# Revit family: Building-SurfaceMountingEnclosures-GEWISS-40CDK-ENCLOSURES_IP65_4X
name_source: partatom
category: Apparecchi elettrici
revit_build: Autodesk Revit 2016 (Build: 20161004_0715(x64)
units: mm (PartAtom-declared; Revit-internal decimal feet)

## family parameters
Condiviso = No
Host = Superficie
Mantenere orientamento annotazione = Sì
Numero OmniClass = 23.80.30.11.17
Punto di calcolo locali = Sì
Quota connettore circolare = Usa diametro
Taglio con vuoti quando caricato = No
Tipo di parte = Normale
Titolo OmniClass = Distribution Boards and Control Panels

## types (1)
- GW40109 - SUR. MOU. DISTRIB.BOARD 72M.(18X4) IP65
    Accessories for insulation restoring = Screwcaps (GW44623) or fixing brackets in resin (GW44621)
    Catalogue = BUILDING
    Catalogue Range = 40 CDK
    Colour = Grey RAL 7035
    Descrizione = SUR. MOU. DISTRIB.BOARD 72M.(18X4) IP65
    Diametro_tubazione = 30 mm  [stored 0.0984252 ft]
    Dimensione modulo = 18 mm  [stored 0.0590551 ft]
    Dispersible power (W) = 89
    Door colour = Smoked Transparent
    EAN code = 8011564062269
    Electrocod = 0321
    Glow Wire Test = 650°C
    H_finestratura = 45 mm  [stored 0.147638 ft]
    H_quadro = 878 mm  [stored 2.88058 ft]
    IDF = e275c9cb-e94d-4235-9db2-dc04921218fb
    IDT = 7e0685bc-1a66-4e12-9668-7a0b7038d661
    IP degree = IP65
    Insulation class = II (according to IEC 61140 standards)
    Insulation voltage: = 1000 V according to EN 62208 both in ac as well as in dc
    L_finestratura = 324 mm  [stored 1.06299 ft]
    L_quadro = 410 mm  [stored 1.34514 ft]
    Max. installable terminal blocks = 4 x 18 modules
    Modello = GW40109
    N.M. = 18
    No. of modules EN 50022 = 72 (18x4)
    No. of modules EN 50022: = 72 (18x4)
    Operating temperature = -25 +60 °C
    Outer dim. LxHxD (mm) = 410x878x160
    Produttore = GEWISS S.p.A.
    Prondita_quadro = 160 mm  [stored 0.524934 ft]
    Prospetto di default = 1219 mm
    QUADRO = FINITURA BIANCA
    Rated current: = 125A
    Rated insulation voltage (Ui) = 1000 V
    Rated voltage = 400V
    SEO = Board
    Shock resistance = IK09
    Spostamento_x_et = 1060 mm
    Standard = EN 60670-1 (CEI 23-48) IEC60670-24 CEI 23-49
    Standard. = EN 60670-1 (CEI 23-48) IEC60670-24 CEI 23-49
    Technical sheet = https://www.gewiss.com
    Thermo-pressure with ball = 70
    Type of material = Halogen-free in compliance with EN 60754-2
    URL = https://www.gewiss.com
    Version file RFA = 18.0
    fase1 = 0 VA
    h_pannello = 718 mm  [stored 2.35564 ft]
    voltaggio_quadro = 0 V

note: source unit labels omitted for Thermo-pressure with ball — the stored unit's dimension contradicts the parameter name (converter mislabeling)

note: [stored X ft] marks values corroborated as IEEE doubles in the binary element streams (Revit-internal decimal feet)

## geometry (parser evidence)
native form markers: Sweep x1
no freeform markers — native parametric forms only
